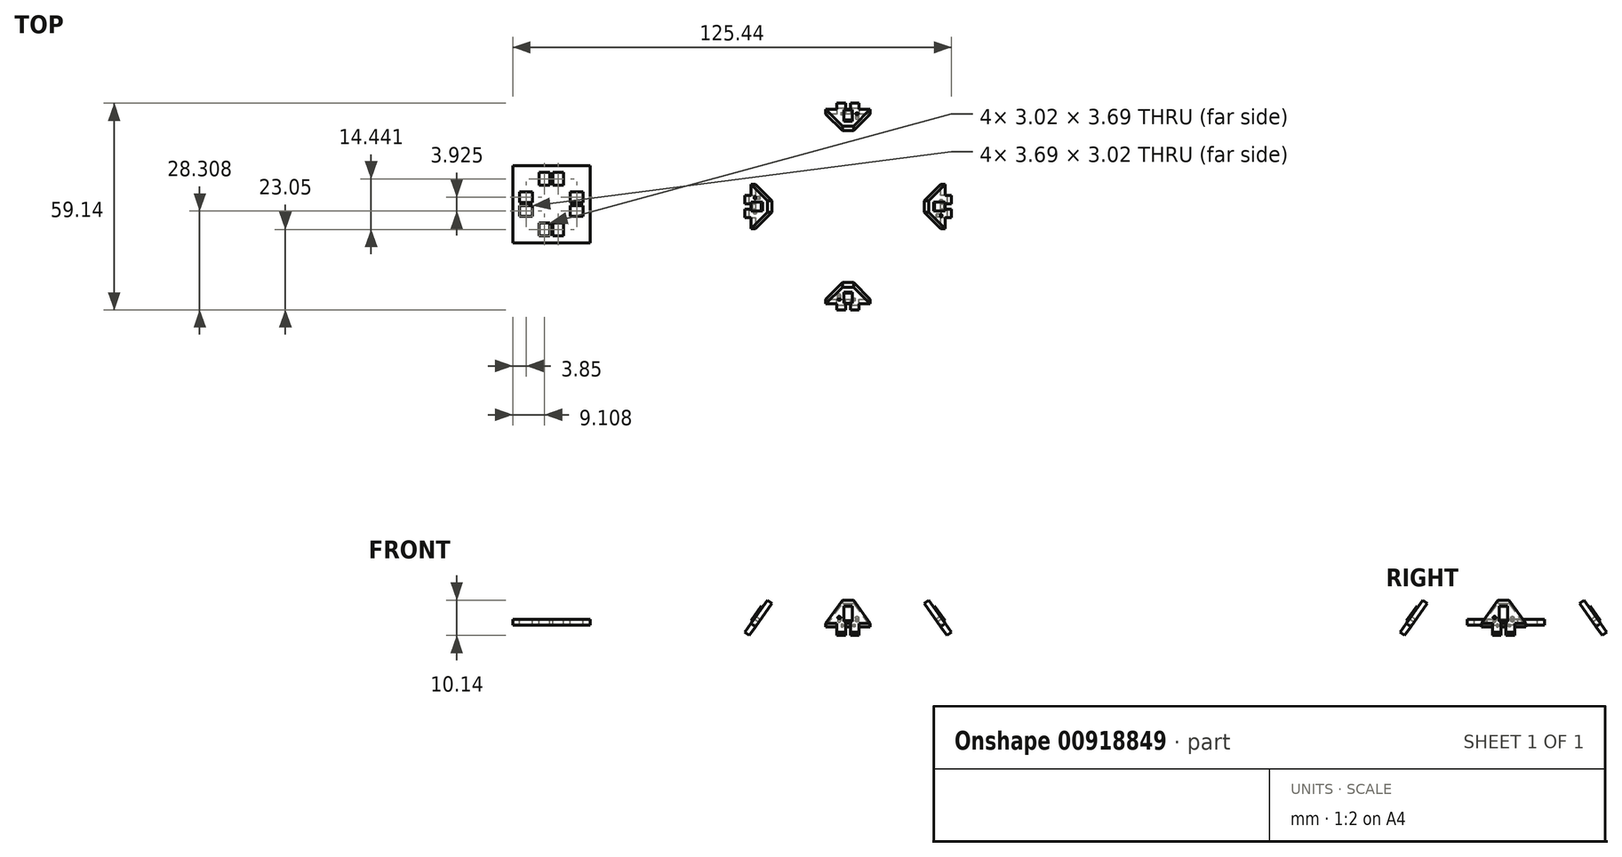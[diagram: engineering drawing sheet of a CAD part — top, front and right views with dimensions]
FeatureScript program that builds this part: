
annotation { "Feature Type Name" : "Feature", "Feature Type Description" : "" }
export const myFeature = defineFeature(function(context is Context, id is Id, definition is map)
    precondition{}
    {
        {
            var Q0;
            Q0=qCreatedBy(makeId("Top.planeOp"),FACE);
            var sketch = newSketch(context, id + "F0", { "sketchPlane" : qUnion([Q0])});
            skLineSegment(sketch, "E0", {"start": v(0, 0) * mm, "end": v(0, 27.35) * mm});
            skLineSegment(sketch, "E1", {"start": v(0, 0) * mm, "end": v(10, 0) * mm});
            skLineSegment(sketch, "E2", {"start": v(10, 0) * mm, "end": v(10, -10) * mm});
            skLineSegment(sketch, "E3", {"start": v(10, -10) * mm, "end": v(0, 0) * mm});
            skLineSegment(sketch, "E4", {"start": v(-60.25, -8.37) * mm, "end": v(-60.25, -4.67) * mm});
            skLineSegment(sketch, "E5", {"start": v(-63.27, -8.37) * mm, "end": v(-63.27, -4.97) * mm});
            skLineSegment(sketch, "E6", {"start": v(-63.27, -4.97) * mm, "end": v(-63.27, -4.67) * mm});
            skLineSegment(sketch, "E7", {"start": v(-63.27, -4.67) * mm, "end": v(-60.25, -4.67) * mm});
            skLineSegment(sketch, "E8", {"start": v(-63.27, -8.37) * mm, "end": v(-60.25, -8.37) * mm});
            skLineSegment(sketch, "E9", {"start": v(-63.27, -8.37) * mm, "end": v(-63.27, -8.07) * mm});
            skLineSegment(sketch, "E10", {"start": v(-59.35, -8.37) * mm, "end": v(-59.35, -4.67) * mm});
            skLineSegment(sketch, "E11", {"start": v(-56.33, -8.37) * mm, "end": v(-56.33, -4.97) * mm});
            skLineSegment(sketch, "E12", {"start": v(-56.33, -4.97) * mm, "end": v(-56.33, -4.67) * mm});
            skLineSegment(sketch, "E13", {"start": v(-56.33, -4.67) * mm, "end": v(-59.35, -4.67) * mm});
            skLineSegment(sketch, "E14", {"start": v(-56.33, -8.37) * mm, "end": v(-59.35, -8.37) * mm});
            skLineSegment(sketch, "E15", {"start": v(-56.33, -8.37) * mm, "end": v(-56.33, -8.07) * mm});
            skLineSegment(sketch, "E16", {"start": v(-50.73, 1.15) * mm, "end": v(-54.43, 1.15) * mm});
            skLineSegment(sketch, "E17", {"start": v(-50.73, 4.17) * mm, "end": v(-54.13, 4.17) * mm});
            skLineSegment(sketch, "E18", {"start": v(-54.13, 4.17) * mm, "end": v(-54.43, 4.17) * mm});
            skLineSegment(sketch, "E19", {"start": v(-54.43, 4.17) * mm, "end": v(-54.43, 1.15) * mm});
            skLineSegment(sketch, "E20", {"start": v(-50.73, 4.17) * mm, "end": v(-50.73, 1.15) * mm});
            skLineSegment(sketch, "E21", {"start": v(-50.73, 4.17) * mm, "end": v(-51.03, 4.17) * mm});
            skLineSegment(sketch, "E22", {"start": v(-50.73, 0.25) * mm, "end": v(-54.43, 0.25) * mm});
            skLineSegment(sketch, "E23", {"start": v(-50.73, -2.77) * mm, "end": v(-54.13, -2.77) * mm});
            skLineSegment(sketch, "E24", {"start": v(-54.13, -2.77) * mm, "end": v(-54.43, -2.77) * mm});
            skLineSegment(sketch, "E25", {"start": v(-54.43, -2.77) * mm, "end": v(-54.43, 0.25) * mm});
            skLineSegment(sketch, "E26", {"start": v(-50.73, -2.77) * mm, "end": v(-50.73, 0.25) * mm});
            skLineSegment(sketch, "E27", {"start": v(-50.73, -2.77) * mm, "end": v(-51.03, -2.77) * mm});
            skLineSegment(sketch, "E28", {"start": v(-60.25, 9.77) * mm, "end": v(-60.25, 6.07) * mm});
            skLineSegment(sketch, "E29", {"start": v(-63.27, 9.77) * mm, "end": v(-63.27, 6.37) * mm});
            skLineSegment(sketch, "E30", {"start": v(-63.27, 6.37) * mm, "end": v(-63.27, 6.07) * mm});
            skLineSegment(sketch, "E31", {"start": v(-63.27, 6.07) * mm, "end": v(-60.25, 6.07) * mm});
            skLineSegment(sketch, "E32", {"start": v(-63.27, 9.77) * mm, "end": v(-60.25, 9.77) * mm});
            skLineSegment(sketch, "E33", {"start": v(-63.27, 9.77) * mm, "end": v(-63.27, 9.47) * mm});
            skLineSegment(sketch, "E34", {"start": v(-59.35, 9.77) * mm, "end": v(-59.35, 6.07) * mm});
            skLineSegment(sketch, "E35", {"start": v(-56.33, 9.77) * mm, "end": v(-56.33, 6.37) * mm});
            skLineSegment(sketch, "E36", {"start": v(-56.33, 6.37) * mm, "end": v(-56.33, 6.07) * mm});
            skLineSegment(sketch, "E37", {"start": v(-56.33, 6.07) * mm, "end": v(-59.35, 6.07) * mm});
            skLineSegment(sketch, "E38", {"start": v(-56.33, 9.77) * mm, "end": v(-59.35, 9.77) * mm});
            skLineSegment(sketch, "E39", {"start": v(-56.33, 9.77) * mm, "end": v(-56.33, 9.47) * mm});
            skLineSegment(sketch, "E40", {"start": v(-68.87, 1.15) * mm, "end": v(-65.17, 1.15) * mm});
            skLineSegment(sketch, "E41", {"start": v(-68.87, 4.17) * mm, "end": v(-65.47, 4.17) * mm});
            skLineSegment(sketch, "E42", {"start": v(-65.47, 4.17) * mm, "end": v(-65.17, 4.17) * mm});
            skLineSegment(sketch, "E43", {"start": v(-65.17, 4.17) * mm, "end": v(-65.17, 1.15) * mm});
            skLineSegment(sketch, "E44", {"start": v(-68.87, 4.17) * mm, "end": v(-68.87, 1.15) * mm});
            skLineSegment(sketch, "E45", {"start": v(-68.87, 4.17) * mm, "end": v(-68.57, 4.17) * mm});
            skLineSegment(sketch, "E46", {"start": v(-68.87, 0.25) * mm, "end": v(-65.17, 0.25) * mm});
            skLineSegment(sketch, "E47", {"start": v(-68.87, -2.77) * mm, "end": v(-65.47, -2.77) * mm});
            skLineSegment(sketch, "E48", {"start": v(-65.47, -2.77) * mm, "end": v(-65.17, -2.77) * mm});
            skLineSegment(sketch, "E49", {"start": v(-65.17, -2.77) * mm, "end": v(-65.17, 0.25) * mm});
            skLineSegment(sketch, "E50", {"start": v(-68.87, -2.77) * mm, "end": v(-68.87, 0.25) * mm});
            skLineSegment(sketch, "E51", {"start": v(-68.87, -2.77) * mm, "end": v(-68.57, -2.77) * mm});
            skLineSegment(sketch, "E52", {"start": v(-48.73, 0.7) * mm, "end": v(-48.73, -10.37) * mm});
            skLineSegment(sketch, "E53", {"start": v(-48.73, -10.37) * mm, "end": v(-59.8, -10.37) * mm});
            skLineSegment(sketch, "E54", {"start": v(-70.87, 0.7) * mm, "end": v(-70.87, -10.37) * mm});
            skLineSegment(sketch, "E55", {"start": v(-70.87, -10.37) * mm, "end": v(-59.8, -10.37) * mm});
            skLineSegment(sketch, "E56", {"start": v(-48.73, 0.7) * mm, "end": v(-48.73, 11.77) * mm});
            skLineSegment(sketch, "E57", {"start": v(-48.73, 11.77) * mm, "end": v(-59.8, 11.77) * mm});
            skLineSegment(sketch, "E58", {"start": v(-70.87, 0.7) * mm, "end": v(-70.87, 11.77) * mm});
            skLineSegment(sketch, "E59", {"start": v(-70.87, 11.77) * mm, "end": v(-59.8, 11.77) * mm});
            skSolve(sketch);
        }
        {
            var Q0;
            Q0=sQuery(id+"F0.wireOp",EDGE,"E0");
            cPlane(context, id + "F1", {"entities" : qUnion([Q0]), "cplaneType" : CPlaneType.LINE_ANGLE, "offset" : 25 * mm, "angle" : 54.74 * degree, "oppositeDirection" : true, "width" : 150 * mm, "height" : 150 * mm});
        }
        {
            var Q0;
            Q0=qCreatedBy(id+"F1.planeOp",FACE);
            var sketch = newSketch(context, id + "F2", { "sketchPlane" : qUnion([Q0])});
            skLineSegment(sketch, "E60", {"start": v(6.35, -2.55) * mm, "end": v(1.62, 5.64) * mm});
            skLineSegment(sketch, "E61", {"start": v(-1.62, 5.64) * mm, "end": v(-6.35, -2.55) * mm});
            skLineSegment(sketch, "E62", {"start": v(3.18, -5.64) * mm, "end": v(0.75, -5.64) * mm});
            skLineSegment(sketch, "E63", {"start": v(-0.75, -5.64) * mm, "end": v(-3.18, -5.64) * mm});
            skLineSegment(sketch, "E64", {"start": v(1.62, 5.64) * mm, "end": v(-1.62, 5.64) * mm});
            skLineSegment(sketch, "E65", {"start": v(-3.18, -5.64) * mm, "end": v(-3.18, -2.55) * mm});
            skLineSegment(sketch, "E66", {"start": v(3.18, -5.64) * mm, "end": v(3.18, -2.55) * mm});
            skLineSegment(sketch, "E67", {"start": v(-6.35, -2.55) * mm, "end": v(-3.18, -2.55) * mm});
            skLineSegment(sketch, "E68", {"start": v(3.18, -2.55) * mm, "end": v(6.35, -2.55) * mm});
            skLineSegment(sketch, "E69", {"start": v(-0.75, -5.64) * mm, "end": v(-0.75, -2.55) * mm});
            skCircle(sketch, "E70", {"center": v(-2.55, -0.48) * mm, "radius": 0.42 * mm});
            skLineSegment(sketch, "E71", {"start": v(-0.75, -2.55) * mm, "end": v(0.75, -2.55) * mm});
            skLineSegment(sketch, "E72", {"start": v(0.75, -2.55) * mm, "end": v(0.75, -5.64) * mm});
            skLineSegment(sketch, "E73", {"start": v(1.96, -2.55) * mm, "end": v(1.46, -2.55) * mm});
            skLineSegment(sketch, "E74", {"start": v(1.46, -2.55) * mm, "end": v(1.46, -2.05) * mm});
            skLineSegment(sketch, "E75", {"start": v(1.46, -2.05) * mm, "end": v(1.96, -2.05) * mm});
            skLineSegment(sketch, "E76", {"start": v(1.96, -2.05) * mm, "end": v(1.96, -2.55) * mm});
            skSolve(sketch);
        }
        {
            var Q0;
            Q0=qSketchRegion(id+"F2",true);
            var Q1;
            Q1=makeQuery(id+"F2.imprint","IMPRINT",FACE,{"disambiguationData":[TD([[makeQuery(id+"F2.imprint","IMPRINT",EDGE,{"derivedFrom":sQuery(id+"F2.wireOp",EDGE,"E73")}),-1.0]])]});
            extrude(context, id + "F3", {"entities" : qUnion([Q0, Q1]), "depth" : 1.6 * mm, "offsetDistance" : 25 * mm});
        }
        {
            var Q0;
            Q0=makeQuery(id+"F2.imprint","IMPRINT",FACE,{"disambiguationData":[TD([[makeQuery(id+"F2.imprint","IMPRINT",EDGE,{"derivedFrom":sQuery(id+"F2.wireOp",EDGE,"E73")}),-1.0]])]});
            extrude(context, id + "F4", {"entities" : qUnion([Q0]), "operationType" : NewBodyOperationType.REMOVE, "depth" : .6 * mm, "offsetDistance" : 25 * mm});
        }
        {
            var Q0;
            Q0=qCreatedBy(makeId("Right.planeOp"),FACE);
            cPlane(context, id + "F5", {"entities" : qUnion([Q0]), "cplaneType" : CPlaneType.OFFSET, "offset" : 25 * mm, "width" : 150 * mm, "height" : 150 * mm});
        }
        {
            var Q0;
            Q0=qCreatedBy(id+"F5.planeOp",FACE);
            var sketch = newSketch(context, id + "F6", { "sketchPlane" : qUnion([Q0])});
            skLineSegment(sketch, "E77", {"start": v(0, 0) * mm, "end": v(0, 26.14) * mm});
            skSolve(sketch);
        }
        {
            var Q0;
            Q0=makeQuery(id+"F3.opExtrude","CAP_FACE",FACE,{"disambiguationData":[OSD([sQuery(id+"F2.wireOp",EDGE,"E60"),sQuery(id+"F2.wireOp",EDGE,"E61"),sQuery(id+"F2.wireOp",EDGE,"E62"),sQuery(id+"F2.wireOp",EDGE,"E63"),sQuery(id+"F2.wireOp",EDGE,"E64"),sQuery(id+"F2.wireOp",EDGE,"E65"),sQuery(id+"F2.wireOp",EDGE,"E66"),sQuery(id+"F2.wireOp",EDGE,"E67"),sQuery(id+"F2.wireOp",EDGE,"E68"),sQuery(id+"F2.wireOp",EDGE,"E69"),sQuery(id+"F2.wireOp",EDGE,"E70"),sQuery(id+"F2.wireOp",EDGE,"E71"),sQuery(id+"F2.wireOp",EDGE,"E72")])],"isStart":false});
            var sketch = newSketch(context, id + "F7", { "sketchPlane" : qUnion([Q0])});
            skPoint(sketch, "E78.0", {"position": v(0, -2.55) * mm});
            skLineSegment(sketch, "E79", {"start": v(0, -2.55) * mm, "end": v(0, -2.55) * mm});
            skLineSegment(sketch, "E80", {"start": v(0, -2.55) * mm, "end": v(0, -1.86) * mm});
            skLineSegment(sketch, "E81", {"start": v(0, -1.86) * mm, "end": v(1.25, -1.86) * mm});
            skLineSegment(sketch, "E82", {"start": v(1.25, -1.86) * mm, "end": v(1.25, 3.24) * mm});
            skLineSegment(sketch, "E83", {"start": v(1.25, 3.24) * mm, "end": v(-1.25, 3.24) * mm});
            skLineSegment(sketch, "E84", {"start": v(-1.25, 3.24) * mm, "end": v(-1.25, -1.86) * mm});
            skLineSegment(sketch, "E85", {"start": v(-1.25, -1.86) * mm, "end": v(0, -1.86) * mm});
            skSolve(sketch);
        }
        {
            var Q0;
            Q0=makeQuery(id+"F7.imprint","IMPRINT",FACE,{"disambiguationData":[TD([[makeQuery(id+"F7.imprint","IMPRINT",EDGE,{"derivedFrom":sQuery(id+"F7.wireOp",EDGE,"E81")}),1.0]])]});
            extrude(context, id + "F8", {"entities" : qUnion([Q0]), "operationType" : NewBodyOperationType.ADD, "depth" : 0.4 * mm, "offsetDistance" : 25 * mm});
        }
        {
            var Q0;
            Q0=makeQuery(id+"F3.opExtrude","SWEPT_BODY",BODY,{"disambiguationData":[OSD([sQuery(id+"F2.wireOp",EDGE,"E60"),sQuery(id+"F2.wireOp",EDGE,"E61"),sQuery(id+"F2.wireOp",EDGE,"E62"),sQuery(id+"F2.wireOp",EDGE,"E63"),sQuery(id+"F2.wireOp",EDGE,"E64"),sQuery(id+"F2.wireOp",EDGE,"E65"),sQuery(id+"F2.wireOp",EDGE,"E66"),sQuery(id+"F2.wireOp",EDGE,"E67"),sQuery(id+"F2.wireOp",EDGE,"E68"),sQuery(id+"F2.wireOp",EDGE,"E69"),sQuery(id+"F2.wireOp",EDGE,"E70"),sQuery(id+"F2.wireOp",EDGE,"E71"),sQuery(id+"F2.wireOp",EDGE,"E72")])]});
            var Q1;
            Q1=sQuery(id+"F6.wireOp",EDGE,"E77");
            circularPattern(context, id + "F9", {"entities" : qUnion([Q0]), "axis" : qUnion([Q1]), "angle" : 360 * degree, "instanceCount" : 4, "equalSpace" : true});
        }
        {
            var Q0;
            Q0=makeQuery(id+"F0.imprint","IMPRINT",FACE,{"disambiguationData":[TD([[makeQuery(id+"F0.imprint","IMPRINT",EDGE,{"derivedFrom":sQuery(id+"F0.wireOp",EDGE,"E4")}),-1.0]])]});
            extrude(context, id + "F10", {"entities" : qUnion([Q0]), "oppositeDirection" : true, "depth" : 1.6 * mm, "offsetDistance" : 25 * mm});
        }
    });
